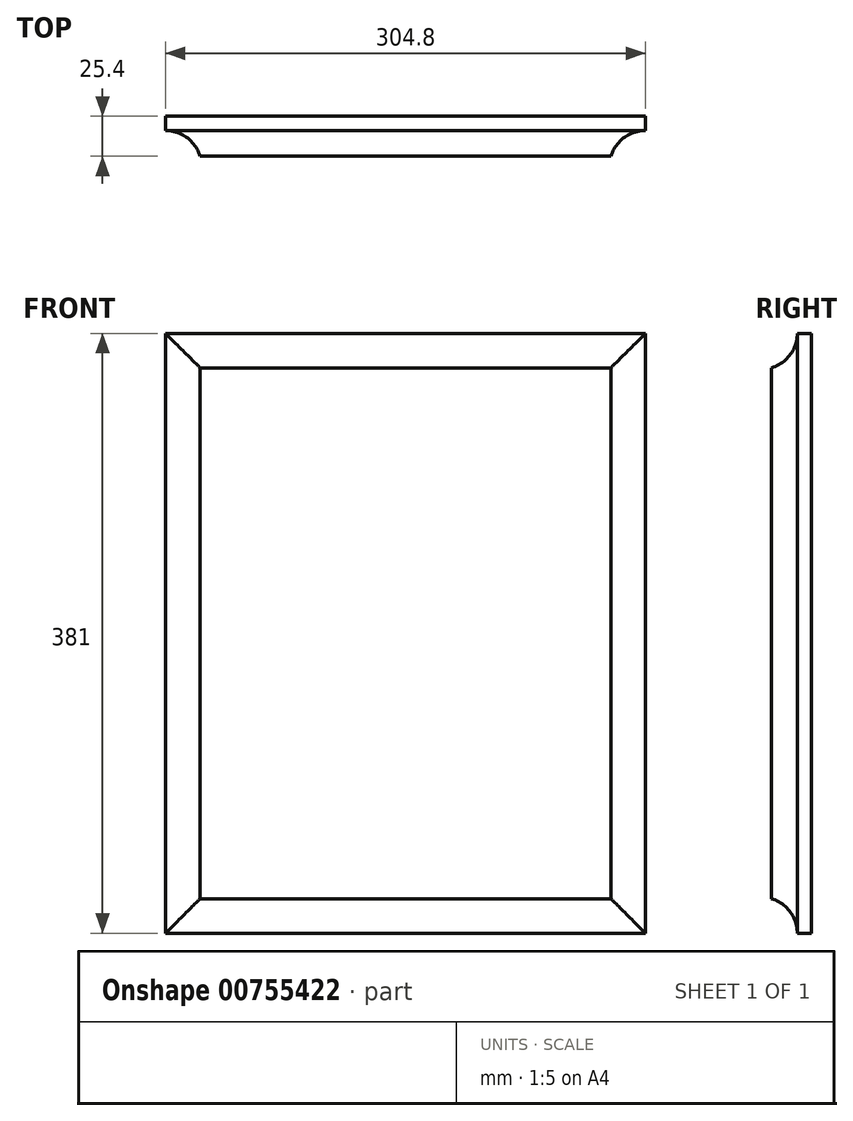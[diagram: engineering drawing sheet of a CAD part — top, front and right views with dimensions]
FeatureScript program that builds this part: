
annotation { "Feature Type Name" : "Feature", "Feature Type Description" : "" }
export const myFeature = defineFeature(function(context is Context, id is Id, definition is map)
    precondition{}
    {
        {
            var Q0;
            Q0=qCreatedBy(makeId("Front.planeOp"),FACE);
            var sketch = newSketch(context, id + "F0", { "sketchPlane" : qUnion([Q0])});
            skLineSegment(sketch, "E0.bottom", {"start": v(-152.4, 190.5) * mm, "end": v(152.4, 190.5) * mm});
            skLineSegment(sketch, "E0.top", {"start": v(-152.4, -190.5) * mm, "end": v(152.4, -190.5) * mm});
            skLineSegment(sketch, "E0.left", {"start": v(-152.4, 190.5) * mm, "end": v(-152.4, -190.5) * mm});
            skLineSegment(sketch, "E0.right", {"start": v(152.4, 190.5) * mm, "end": v(152.4, -190.5) * mm});
            skPoint(sketch, "E0.middle", {"position": v(0, 0) * mm});
            skSolve(sketch);
        }
        {
            var Q0;
            Q0=makeQuery(id+"F0.imprint","IMPRINT",FACE,{"disambiguationData":[TD([[makeQuery(id+"F0.imprint","IMPRINT",EDGE,{"derivedFrom":sQuery(id+"F0.wireOp",EDGE,"E0.bottom")}),-1.0]])]});
            extrude(context, id + "F1", {"entities" : qUnion([Q0]), "endBound" : BoundingType.SYMMETRIC, "depth" : 25.4 * mm, "offsetDistance" : 25.4 * mm});
        }
        {
            var Q0;
            Q0=makeQuery(id+"F1.opExtrude","SWEPT_FACE",FACE,{"disambiguationData":[OSD([sQuery(id+"F0.wireOp",EDGE,"E0.top")])]});
            var sketch = newSketch(context, id + "F2", { "sketchPlane" : qUnion([Q0])});
            skArc(sketch, "E1", {"start": v(-152.4, -3.73) * mm, "mid": v(-138.72, 0.87) * mm, "end": v(-130.47, 12.7) * mm});
            skLineSegment(sketch, "E2", {"start": v(-152.4, -3.73) * mm, "end": v(-152.4, 12.7) * mm});
            skLineSegment(sketch, "E3", {"start": v(-152.4, 12.7) * mm, "end": v(-130.47, 12.7) * mm});
            skSolve(sketch);
        }
        {
            var Q0;
            Q0=makeQuery(id+"F2.imprint","IMPRINT",FACE,{"disambiguationData":[TD([[makeQuery(id+"F2.imprint","IMPRINT",EDGE,{"derivedFrom":sQuery(id+"F2.wireOp",EDGE,"E1")}),1.0]])]});
            var Q1;
            Q1=makeQuery(id+"F1.opExtrude","CAP_EDGE",EDGE,{"disambiguationData":[OSD([sQuery(id+"F0.wireOp",EDGE,"E0.left")])],"isStart":false});
            var Q2;
            Q2=makeQuery(id+"F1.opExtrude","CAP_EDGE",EDGE,{"disambiguationData":[OSD([sQuery(id+"F0.wireOp",EDGE,"E0.bottom")])],"isStart":false});
            var Q3;
            Q3=makeQuery(id+"F1.opExtrude","CAP_EDGE",EDGE,{"disambiguationData":[OSD([sQuery(id+"F0.wireOp",EDGE,"E0.right")])],"isStart":false});
            var Q4;
            Q4=makeQuery(id+"F1.opExtrude","CAP_EDGE",EDGE,{"disambiguationData":[OSD([sQuery(id+"F0.wireOp",EDGE,"E0.top")])],"isStart":false});
            sweep(context, id + "F3", {"operationType" : NewBodyOperationType.REMOVE, "profiles" : qUnion([Q0]), "path" : qUnion([Q1, Q2, Q3, Q4])});
        }
    });
